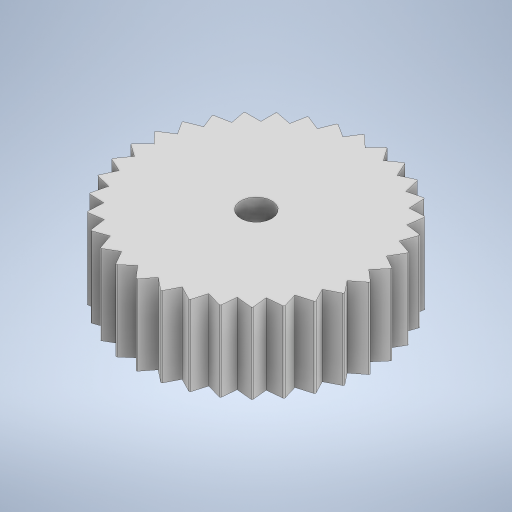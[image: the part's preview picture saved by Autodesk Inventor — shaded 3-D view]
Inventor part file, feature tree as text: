
AUTODESK INVENTOR PART (.ipt)
format: ipt  version: 2024 (Build 280153000, 153)  size: 397,824 bytes
history: native  units: in
note: dims shown in document units (in); Inventor stores cm internally (conversion verified against a paired STEP export)
features: extrude x3, sketch x3, pattern_circular x2, fillet x1
ambient origin geometry x8: Origin, YZ Plane, XZ Plane, XY Plane, X Axis, Y Axis, Z Axis, Center Point
bodies: Solid1 (feature_tree)
feature tree (9):
  extrude  "Extrusion1"  Depth=0.315in TaperAngle=0.0deg
  extrude  "Extrusion2"  Depth=0.315in TaperAngle=0.0deg
  pattern_circular  "Circular Pattern1"  Count=33 Angle=360.0deg
  fillet  "Fillet1"  Radius=0.0039in
  pattern_circular  "Circular Pattern2"  Count=33 Angle=360.0deg
  extrude  "Extrusion3"  Depth=0.315in TaperAngle=0.0deg
  sketch  "Sketch1"  dims[d0=0.9449in d1=0.315in d2=0.0in]
  sketch  "Sketch2"  dims[d3=12.9921in d5=360.0deg d7=0.315in d8=0.0in d9=12.9921in d10=360.0deg d12=0.0039in d13=12.9921in d14=360.0deg]
  sketch  "Sketch3"  dims[d16=0.122in d17=0.315in d18=0.0in]
